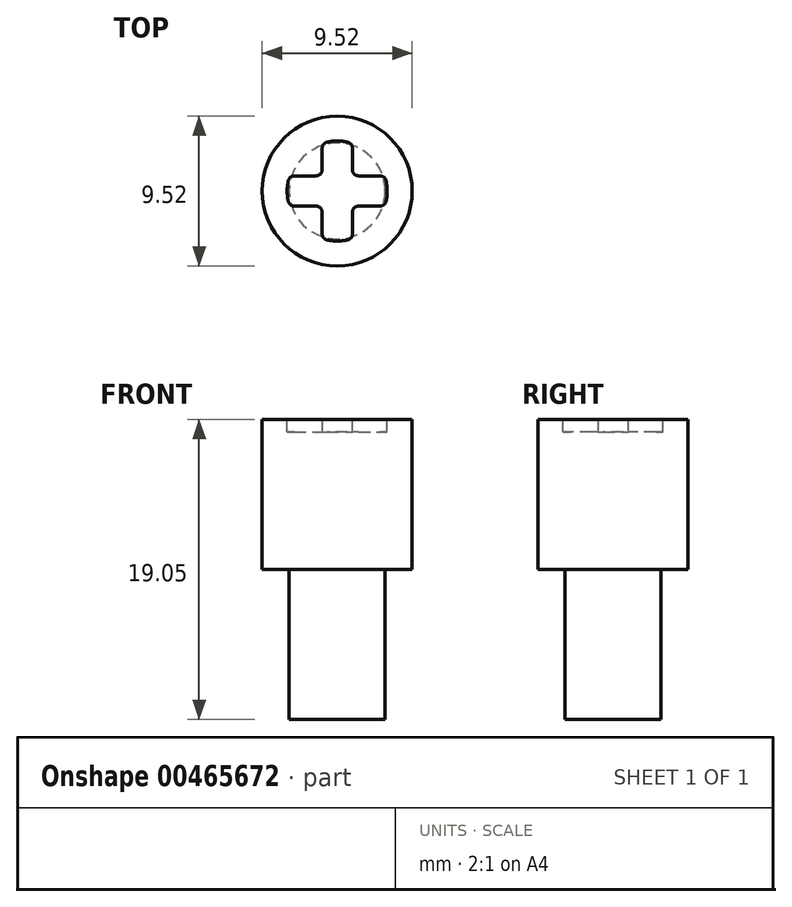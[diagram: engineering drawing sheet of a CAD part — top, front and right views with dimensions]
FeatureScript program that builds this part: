
annotation { "Feature Type Name" : "Feature", "Feature Type Description" : "" }
export const myFeature = defineFeature(function(context is Context, id is Id, definition is map)
    precondition{}
    {
        {
            var Q0;
            Q0=qCreatedBy(makeId("Top.planeOp"),FACE);
            var sketch = newSketch(context, id + "F0", { "sketchPlane" : qUnion([Q0])});
            skCircle(sketch, "E0", {"center": v(0, 0) * mm, "radius": 3.05 * mm});
            skSolve(sketch);
        }
        {
            var Q0;
            Q0 = qSketchRegion(id + "F0", true);
            extrude(context, id + "F1", {"entities" : qUnion([Q0]), "endBound" : BoundingType.SYMMETRIC, "depth" : 9.52 * mm});
        }
        {
            var Q0;
            Q0=makeQuery(id+"F1.opExtrude","CAP_FACE",FACE,{"disambiguationData":[OSD([sQuery(id+"F0.wireOp",EDGE,"E0")])],"isStart":false});
            var sketch = newSketch(context, id + "F2", { "sketchPlane" : qUnion([Q0])});
            skCircle(sketch, "E1", {"center": v(0, 0) * mm, "radius": 4.76 * mm});
            skSolve(sketch);
        }
        {
            var Q0;
            Q0 = qSketchRegion(id + "F2", true);
            extrude(context, id + "F3", {"entities" : qUnion([Q0]), "operationType" : NewBodyOperationType.ADD, "depth" : 9.52 * mm});
        }
        {
            var Q0;
            Q0=makeQuery(id+"F3.opExtrude","CAP_FACE",FACE,{"disambiguationData":[OSD([sQuery(id+"F2.wireOp",EDGE,"E1")])],"isStart":false});
            var sketch = newSketch(context, id + "F4", { "sketchPlane" : qUnion([Q0])});
            skLineSegment(sketch, "E2.0", {"start": v(-0.95, 3.03) * mm, "end": v(-0.95, 0.97) * mm});
            skLineSegment(sketch, "E3.0", {"start": v(0.97, 3.02) * mm, "end": v(0.97, 0.97) * mm});
            skLineSegment(sketch, "E4.0", {"start": v(-3.03, -0.95) * mm, "end": v(-0.95, -0.95) * mm});
            skLineSegment(sketch, "E5.0", {"start": v(-3.02, 0.97) * mm, "end": v(-0.95, 0.97) * mm});
            skArc(sketch, "E6.0", {"start": v(-3.02, 0.97) * mm, "mid": v(-3.17, 0) * mm, "end": v(-3.03, -0.95) * mm});
            skLineSegment(sketch, "E7.trimOffspring", {"start": v(-0.95, -0.95) * mm, "end": v(-0.95, -3.03) * mm});
            skPoint(sketch, "E8.orphan", {"position": v(-3.17, 0) * mm});
            skLineSegment(sketch, "E9.trimOffspring", {"start": v(0.97, 0.97) * mm, "end": v(3.02, 0.97) * mm});
            skPoint(sketch, "E10.start.orphan", {"position": v(0, 3.17) * mm});
            skLineSegment(sketch, "E11.trimOffspring", {"start": v(0.97, -0.95) * mm, "end": v(3.03, -0.95) * mm});
            skLineSegment(sketch, "E12.trimOffspring", {"start": v(0.97, -0.95) * mm, "end": v(0.97, -3.02) * mm});
            skArc(sketch, "E13.trimOffspring", {"start": v(0.97, 3.02) * mm, "mid": v(0, 3.17) * mm, "end": v(-0.95, 3.03) * mm});
            skArc(sketch, "E14.trimOffspring", {"start": v(3.03, -0.95) * mm, "mid": v(3.17, 0) * mm, "end": v(3.02, 0.97) * mm});
            skArc(sketch, "E15.trimOffspring", {"start": v(-0.95, -3.03) * mm, "mid": v(0, -3.17) * mm, "end": v(0.97, -3.02) * mm});
            skSolve(sketch);
        }
        {
            var Q0;
            Q0 = qSketchRegion(id + "F4", true);
            extrude(context, id + "F5", {"entities" : qUnion([Q0]), "operationType" : NewBodyOperationType.REMOVE, "oppositeDirection" : true, "depth" : 0.8 * mm});
        }
        {
            var Q0;
            Q0=makeQuery(id+"F5.boolean.opBoolean","COPY",EDGE,{"derivedFrom":makeQuery(id+"F5.opExtrude","SWEPT_EDGE",EDGE,{"disambiguationData":[OSD([sQuery(id+"F4.wireOp",EDGE,"E2.0"),sQuery(id+"F4.wireOp",EDGE,"E5.0")])]})});
            var Q1;
            Q1=makeQuery(id+"F5.boolean.opBoolean","COPY",EDGE,{"derivedFrom":makeQuery(id+"F5.opExtrude","SWEPT_EDGE",EDGE,{"disambiguationData":[OSD([sQuery(id+"F4.wireOp",EDGE,"E3.0"),sQuery(id+"F4.wireOp",EDGE,"E9.trimOffspring")])]})});
            var Q2;
            Q2=makeQuery(id+"F5.boolean.opBoolean","COPY",EDGE,{"derivedFrom":makeQuery(id+"F5.opExtrude","SWEPT_EDGE",EDGE,{"disambiguationData":[OSD([sQuery(id+"F4.wireOp",EDGE,"E11.trimOffspring"),sQuery(id+"F4.wireOp",EDGE,"E12.trimOffspring")])]})});
            var Q3;
            Q3=makeQuery(id+"F5.boolean.opBoolean","COPY",EDGE,{"derivedFrom":makeQuery(id+"F5.opExtrude","SWEPT_EDGE",EDGE,{"disambiguationData":[OSD([sQuery(id+"F4.wireOp",EDGE,"E4.0"),sQuery(id+"F4.wireOp",EDGE,"E7.trimOffspring")])]})});
            var Q4;
            Q4=makeQuery(id+"F5.boolean.opBoolean","COPY",EDGE,{"derivedFrom":makeQuery(id+"F5.opExtrude","SWEPT_EDGE",EDGE,{"disambiguationData":[OSD([sQuery(id+"F2.wireOp",EDGE,"E1"),sQuery(id+"F4.wireOp",EDGE,"E4.0"),sQuery(id+"F4.wireOp",EDGE,"E6.0")])]})});
            var Q5;
            Q5=makeQuery(id+"F5.boolean.opBoolean","COPY",EDGE,{"derivedFrom":makeQuery(id+"F5.opExtrude","SWEPT_EDGE",EDGE,{"disambiguationData":[OSD([sQuery(id+"F2.wireOp",EDGE,"E1"),sQuery(id+"F4.wireOp",EDGE,"E5.0"),sQuery(id+"F4.wireOp",EDGE,"E6.0")])]})});
            var Q6;
            Q6=makeQuery(id+"F5.boolean.opBoolean","COPY",EDGE,{"derivedFrom":makeQuery(id+"F5.opExtrude","SWEPT_EDGE",EDGE,{"disambiguationData":[OSD([sQuery(id+"F2.wireOp",EDGE,"E1"),sQuery(id+"F4.wireOp",EDGE,"E12.trimOffspring"),sQuery(id+"F4.wireOp",EDGE,"E15.trimOffspring")])]})});
            var Q7;
            Q7=makeQuery(id+"F5.boolean.opBoolean","COPY",EDGE,{"derivedFrom":makeQuery(id+"F5.opExtrude","SWEPT_EDGE",EDGE,{"disambiguationData":[OSD([sQuery(id+"F2.wireOp",EDGE,"E1"),sQuery(id+"F4.wireOp",EDGE,"E11.trimOffspring"),sQuery(id+"F4.wireOp",EDGE,"E14.trimOffspring")])]})});
            var Q8;
            Q8=makeQuery(id+"F5.boolean.opBoolean","COPY",EDGE,{"derivedFrom":makeQuery(id+"F5.opExtrude","SWEPT_EDGE",EDGE,{"disambiguationData":[OSD([sQuery(id+"F2.wireOp",EDGE,"E1"),sQuery(id+"F4.wireOp",EDGE,"E9.trimOffspring"),sQuery(id+"F4.wireOp",EDGE,"E14.trimOffspring")])]})});
            var Q9;
            Q9=makeQuery(id+"F5.boolean.opBoolean","COPY",EDGE,{"derivedFrom":makeQuery(id+"F5.opExtrude","SWEPT_EDGE",EDGE,{"disambiguationData":[OSD([sQuery(id+"F2.wireOp",EDGE,"E1"),sQuery(id+"F4.wireOp",EDGE,"E3.0"),sQuery(id+"F4.wireOp",EDGE,"E13.trimOffspring")])]})});
            var Q10;
            Q10=makeQuery(id+"F5.boolean.opBoolean","COPY",EDGE,{"derivedFrom":makeQuery(id+"F5.opExtrude","SWEPT_EDGE",EDGE,{"disambiguationData":[OSD([sQuery(id+"F2.wireOp",EDGE,"E1"),sQuery(id+"F4.wireOp",EDGE,"E2.0"),sQuery(id+"F4.wireOp",EDGE,"E13.trimOffspring")])]})});
            var Q11;
            Q11=makeQuery(id+"F5.boolean.opBoolean","COPY",EDGE,{"derivedFrom":makeQuery(id+"F5.opExtrude","SWEPT_EDGE",EDGE,{"disambiguationData":[OSD([sQuery(id+"F2.wireOp",EDGE,"E1"),sQuery(id+"F4.wireOp",EDGE,"E7.trimOffspring"),sQuery(id+"F4.wireOp",EDGE,"E15.trimOffspring")])]})});
            fillet(context, id + "F6", {"entities" : qUnion([Q0, Q1, Q2, Q3, Q4, Q5, Q6, Q7, Q8, Q9, Q10, Q11]), "radius" : 0.4 * mm, "tangentPropagation" : true, "allowEdgeOverflow" : false});
        }
    });
